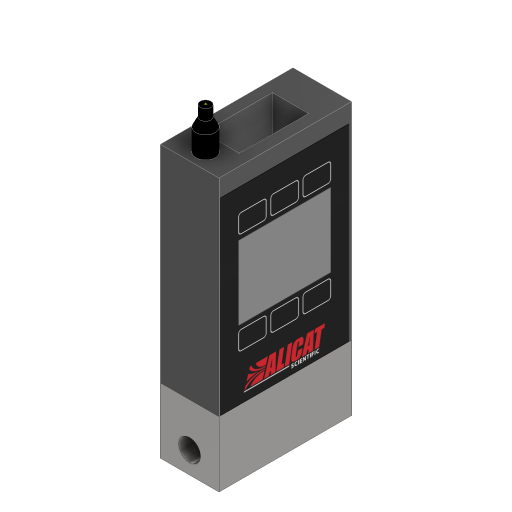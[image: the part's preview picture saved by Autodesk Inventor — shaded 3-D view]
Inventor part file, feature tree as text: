
AUTODESK INVENTOR PART (.ipt)
format: ipt  version: 2024 (Build 280153000, 153)  size: 252,928 bytes
history: native  units: mm
features: extrude x8, other x6, sketch x6, split x1, plane x1, loft x1, boolean_combine x1
ambient origin geometry x8: Origin, YZ Plane, XZ Plane, XY Plane, X Axis, Y Axis, Z Axis, Center Point
bodies: Solid1 (feature_tree), Solid4 (feature_tree), Solid5 (feature_tree), Solid2 (feature_tree), Solid3 (feature_tree)
feature tree (24):
  extrude  "Extrusion1"  Depth=61.0mm
  split  "Split1"
  extrude  "Extrusion2"  Depth=30.0mm
  extrude  "Extrusion3"  Depth=10.0mm
  other  "Decal2"
  extrude  "Extrusion4"  Depth=4.0mm
  extrude  "Extrusion5"  Depth=10.0mm
  extrude  "Extrusion6"  Depth=8.0mm
  extrude  "Extrusion7"  Depth=8.0mm
  plane  "Work Plane4"
  extrude  "Extrusion8"  Depth=4.0mm
  loft  "Loft1"
  boolean_combine  "Combine1"
  other  "Decal3"
  sketch  "Sketch3"  dims[d0=27.0mm d1=61.0mm]
  sketch  "Sketch4"  dims[d2=125.0mm d3=0.0mm d4=30.0mm]
  sketch  "Sketch12"  dims[d5=10.0mm d6=10.0mm]
  other  "Image2"
  sketch  "Sketch15"  dims[d7=4.0mm d8=4.0mm]
  sketch  "Sketch17"  dims[d9=10.0mm d10=0.0mm d11=10.0mm]
  other  "Edges1"
  other  "Edges2"
  sketch  "Sketch19"  dims[d12=10.0mm d13=0.0mm d14=8.0mm d15=8.0mm d16=4.0mm d39=30.5mm d40=16.65mm d41=31.8mm d42=16.2mm d43=0.0mm d44=7.3mm d45=8.0mm d46=1.0mm d47=0.0mm d48=6.0mm d49=7.0mm d50=0.0mm d51=9.0mm d52=10.0mm d53=0.0mm d54=4.0mm d55=5.0mm d56=5.0mm d57=0.0mm d58=0.0mm d59=90.0deg d60=0.0mm d61=90.0deg]
  other  "Image3"
